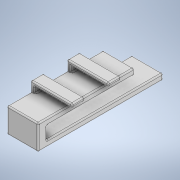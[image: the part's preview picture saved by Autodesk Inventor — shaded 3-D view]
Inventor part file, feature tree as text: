
AUTODESK INVENTOR PART (.ipt)
format: ipt  version: 2020 (Build 240168000, 168)  size: 245,248 bytes
history: native  units: in
note: dims shown in document units (in); Inventor stores cm internally (conversion verified against a paired STEP export)
features: extrude x5, sketch x5, fillet x1
ambient origin geometry x8: Origin, YZ Plane, XZ Plane, XY Plane, X Axis, Y Axis, Z Axis, Center Point
bodies: Solid1 (feature_tree)
feature tree (11):
  extrude  "Extrusion1"  Depth=1.0in
  extrude  "Extrusion2"  Depth=0.15in TaperAngle=0.0deg
  extrude  "Extrusion3"  Depth=0.19in
  extrude  "Extrusion4"  Depth=0.1in
  extrude  "Extrusion5"  Depth=0.01in
  fillet  "Fillet1"  Radius=0.1in
  sketch  "Sketch1"  dims[d0=0.25in d1=1.0in]
  sketch  "Sketch2"  dims[d2=0.05in d3=0.0in d4=0.15in d5=0.0in]
  sketch  "Sketch4"  dims[d6=0.7in d7=0.0in d8=0.19in]
  sketch  "Sketch5"  dims[d9=0.03in d10=0.1in]
  sketch  "Sketch6"  dims[d11=0.19in d12=0.03in d13=0.1in d14=0.08in d15=0.0in d16=0.03in d17=0.03in d18=0.3in d19=0.0in d20=0.01in]
